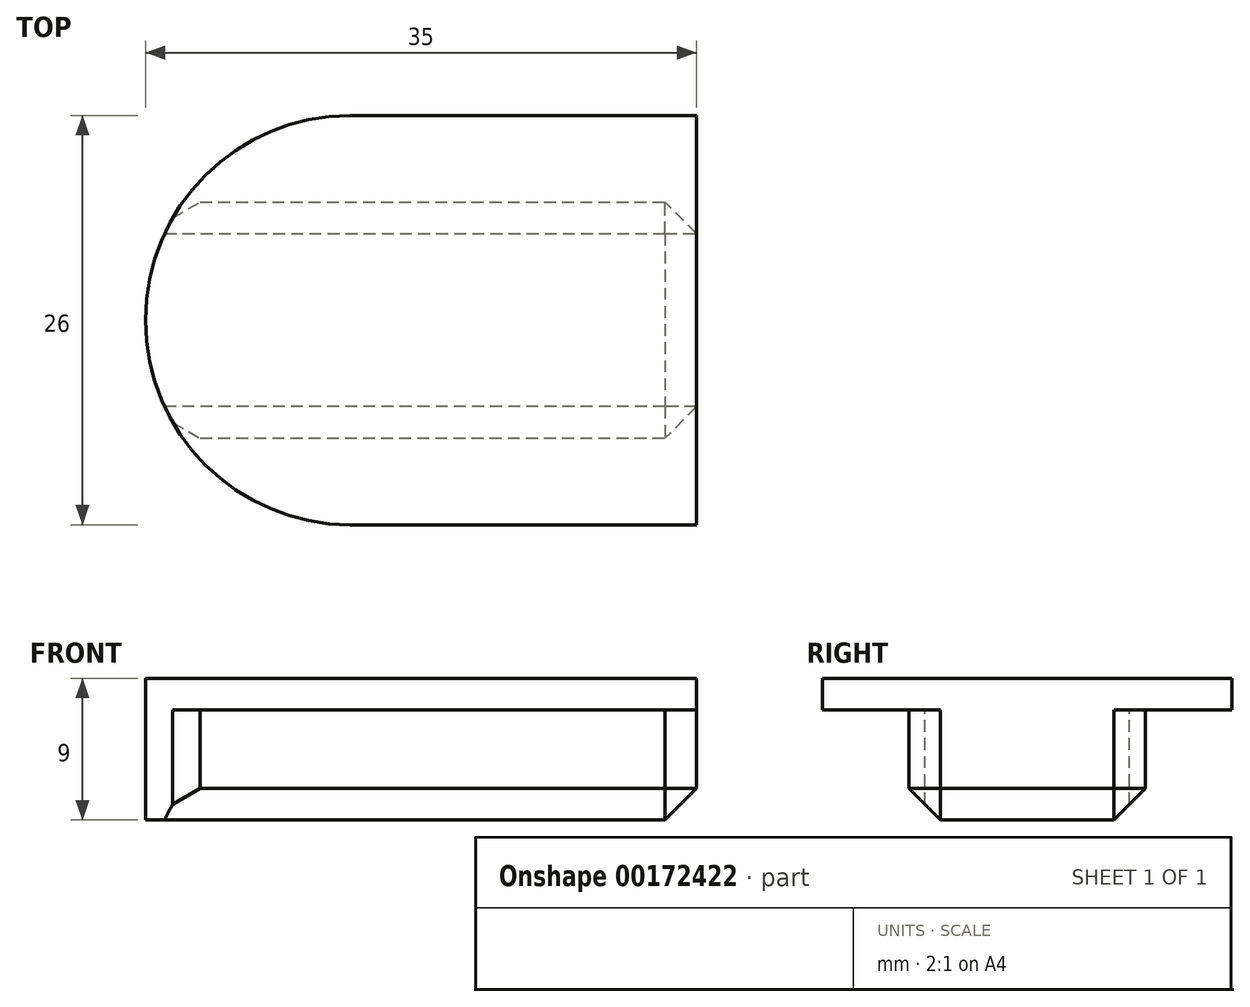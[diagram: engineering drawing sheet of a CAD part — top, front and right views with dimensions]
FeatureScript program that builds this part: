
annotation { "Feature Type Name" : "Feature", "Feature Type Description" : "" }
export const myFeature = defineFeature(function(context is Context, id is Id, definition is map)
    precondition{}
    {
        {
            var Q0;
            Q0=qCreatedBy(makeId("Top.planeOp"),FACE);
            var sketch = newSketch(context, id + "F0", { "sketchPlane" : qUnion([Q0])});
            skLineSegment(sketch, "E0.bottom", {"start": v(-17.5, 13) * mm, "end": v(17.5, 13) * mm});
            skLineSegment(sketch, "E0.top", {"start": v(-17.5, -13) * mm, "end": v(17.5, -13) * mm});
            skLineSegment(sketch, "E0.left", {"start": v(-17.5, 13) * mm, "end": v(-17.5, -13) * mm});
            skLineSegment(sketch, "E0.right", {"start": v(17.5, 13) * mm, "end": v(17.5, -13) * mm});
            skPoint(sketch, "E0.middle", {"position": v(0, 0) * mm});
            skSolve(sketch);
        }
        {
            var Q0;
            Q0 = qSketchRegion(id + "F0", true);
            extrude(context, id + "F1", {"entities" : qUnion([Q0]), "depth" : 2 * mm});
        }
        {
            var Q0;
            Q0=makeQuery(id+"F1.opExtrude","CAP_FACE",FACE,{"disambiguationData":[OSD([sQuery(id+"F0.wireOp",EDGE,"E0.bottom"),sQuery(id+"F0.wireOp",EDGE,"E0.top"),sQuery(id+"F0.wireOp",EDGE,"E0.left"),sQuery(id+"F0.wireOp",EDGE,"E0.right")])],"isStart":true});
            var sketch = newSketch(context, id + "F2", { "sketchPlane" : qUnion([Q0])});
            skLineSegment(sketch, "E1.bottom", {"start": v(-17.5, 7.5) * mm, "end": v(17.5, 7.5) * mm});
            skLineSegment(sketch, "E1.top", {"start": v(-17.5, -7.5) * mm, "end": v(17.5, -7.5) * mm});
            skLineSegment(sketch, "E1.left", {"start": v(-17.5, 7.5) * mm, "end": v(-17.5, -7.5) * mm});
            skLineSegment(sketch, "E1.right", {"start": v(17.5, 7.5) * mm, "end": v(17.5, -7.5) * mm});
            skPoint(sketch, "E1.middle", {"position": v(0, 0) * mm});
            skSolve(sketch);
        }
        {
            var Q0;
            Q0 = qSketchRegion(id + "F2", true);
            extrude(context, id + "F3", {"entities" : qUnion([Q0]), "operationType" : NewBodyOperationType.ADD, "depth" : 7 * mm});
        }
        {
            var Q0;
            Q0=makeQuery(id+"F1.opExtrude","SWEPT_EDGE",EDGE,{"disambiguationData":[OSD([sQuery(id+"F0.wireOp",EDGE,"E0.bottom"),sQuery(id+"F0.wireOp",EDGE,"E0.left")])]});
            var Q1;
            Q1=makeQuery(id+"F1.opExtrude","SWEPT_EDGE",EDGE,{"disambiguationData":[OSD([sQuery(id+"F0.wireOp",EDGE,"E0.top"),sQuery(id+"F0.wireOp",EDGE,"E0.left")])]});
            fillet(context, id + "F4", {"entities" : qUnion([Q0, Q1]), "radius" : 13 * mm, "tangentPropagation" : true, "allowEdgeOverflow" : false});
        }
        {
            var Q0;
            Q0=makeQuery(id+"F3.opExtrude","CAP_EDGE",EDGE,{"disambiguationData":[OSD([sQuery(id+"F2.wireOp",EDGE,"E1.bottom")])],"isStart":false});
            var Q1;
            Q1=makeQuery(id+"F3.opExtrude","CAP_EDGE",EDGE,{"disambiguationData":[OSD([sQuery(id+"F2.wireOp",EDGE,"E1.top")])],"isStart":false});
            var Q2;
            Q2=makeQuery(id+"F3.opExtrude","CAP_EDGE",EDGE,{"disambiguationData":[OSD([sQuery(id+"F2.wireOp",EDGE,"E1.left")])],"isStart":false});
            var Q3;
            Q3=makeQuery(id+"F3.opExtrude","CAP_EDGE",EDGE,{"disambiguationData":[OSD([sQuery(id+"F2.wireOp",EDGE,"E1.right")])],"isStart":false});
            var Q4;
            {var subQ0=sQuery(id+"F0.wireOp",EDGE,"E0.left");var subQ1=sQuery(id+"F0.wireOp",EDGE,"E0.top");Q4=makeQuery(id+"F3.boolean.opBoolean","SPLIT",EDGE,{"disambiguationData":[TD([makeQuery(id+"F1.opExtrude","SWEPT_FACE",FACE,{"disambiguationData":[OSD([subQ1])]})])],"derivedFrom":makeQuery(id+"F1.opExtrude","CAP_EDGE",EDGE,{"disambiguationData":[OSD([subQ0])],"isStart":true})});}
            var Q5;
            {var subQ0=sQuery(id+"F0.wireOp",EDGE,"E0.left");var subQ1=sQuery(id+"F0.wireOp",EDGE,"E0.bottom");Q5=makeQuery(id+"F3.boolean.opBoolean","SPLIT",EDGE,{"disambiguationData":[TD([makeQuery(id+"F1.opExtrude","SWEPT_FACE",FACE,{"disambiguationData":[OSD([subQ1])]})])],"derivedFrom":makeQuery(id+"F1.opExtrude","CAP_EDGE",EDGE,{"disambiguationData":[OSD([subQ0])],"isStart":true})});}
            var Q6;
            Q6=makeQuery(id+"F3.opExtrude","SWEPT_EDGE",EDGE,{"disambiguationData":[OSD([sQuery(id+"F0.wireOp",EDGE,"E0.left"),sQuery(id+"F2.wireOp",EDGE,"E1.bottom"),sQuery(id+"F2.wireOp",EDGE,"E1.left")])]});
            var Q7;
            Q7=makeQuery(id+"F3.opExtrude","SWEPT_EDGE",EDGE,{"disambiguationData":[OSD([sQuery(id+"F0.wireOp",EDGE,"E0.left"),sQuery(id+"F2.wireOp",EDGE,"E1.top"),sQuery(id+"F2.wireOp",EDGE,"E1.left")])]});
            var Q8;
            Q8=makeQuery(id+"F3.opExtrude","SWEPT_EDGE",EDGE,{"disambiguationData":[OSD([sQuery(id+"F0.wireOp",EDGE,"E0.right"),sQuery(id+"F2.wireOp",EDGE,"E1.bottom"),sQuery(id+"F2.wireOp",EDGE,"E1.right")])]});
            var Q9;
            Q9=makeQuery(id+"F3.opExtrude","SWEPT_EDGE",EDGE,{"disambiguationData":[OSD([sQuery(id+"F0.wireOp",EDGE,"E0.right"),sQuery(id+"F2.wireOp",EDGE,"E1.top"),sQuery(id+"F2.wireOp",EDGE,"E1.right")])]});
            var Q10;
            Q10=makeQuery(id+"F4.opFillet","BLEND_EDGE",EDGE,{"blendedFrom":[makeQuery(id+"F1.opExtrude","SWEPT_EDGE",EDGE,{"disambiguationData":[OSD([sQuery(id+"F0.wireOp",EDGE,"E0.bottom"),sQuery(id+"F0.wireOp",EDGE,"E0.left")])]}),makeQuery(id+"F3.opExtrude","SWEPT_FACE",FACE,{"disambiguationData":[OSD([sQuery(id+"F2.wireOp",EDGE,"E1.top")])]})],"blendedInto":[makeQuery(id+"F3.opExtrude","SWEPT_FACE",FACE,{"disambiguationData":[OSD([sQuery(id+"F2.wireOp",EDGE,"E1.top")])]})]});
            var Q11;
            Q11=makeQuery(id+"F4.opFillet","BLEND_EDGE",EDGE,{"blendedFrom":[makeQuery(id+"F1.opExtrude","SWEPT_EDGE",EDGE,{"disambiguationData":[OSD([sQuery(id+"F0.wireOp",EDGE,"E0.top"),sQuery(id+"F0.wireOp",EDGE,"E0.left")])]}),makeQuery(id+"F3.opExtrude","SWEPT_FACE",FACE,{"disambiguationData":[OSD([sQuery(id+"F2.wireOp",EDGE,"E1.bottom")])]})],"blendedInto":[makeQuery(id+"F3.opExtrude","SWEPT_FACE",FACE,{"disambiguationData":[OSD([sQuery(id+"F2.wireOp",EDGE,"E1.bottom")])]})]});
            var Q12;
            Q12=makeQuery(id+"F4.opFillet","BLEND_EDGE",EDGE,{"blendedFrom":[makeQuery(id+"F1.opExtrude","SWEPT_EDGE",EDGE,{"disambiguationData":[OSD([sQuery(id+"F0.wireOp",EDGE,"E0.top"),sQuery(id+"F0.wireOp",EDGE,"E0.left")])]}),makeQuery(id+"F3.opExtrude","CAP_FACE",FACE,{"disambiguationData":[OSD([sQuery(id+"F2.wireOp",EDGE,"E1.bottom"),sQuery(id+"F2.wireOp",EDGE,"E1.top"),sQuery(id+"F2.wireOp",EDGE,"E1.left"),sQuery(id+"F2.wireOp",EDGE,"E1.right")])],"isStart":false})],"blendedInto":[makeQuery(id+"F3.opExtrude","CAP_FACE",FACE,{"disambiguationData":[OSD([sQuery(id+"F2.wireOp",EDGE,"E1.bottom"),sQuery(id+"F2.wireOp",EDGE,"E1.top"),sQuery(id+"F2.wireOp",EDGE,"E1.left"),sQuery(id+"F2.wireOp",EDGE,"E1.right")])],"isStart":false})]});
            chamfer(context, id + "F5", {"entities" : qUnion([Q0, Q1, Q2, Q3, Q4, Q5, Q6, Q7, Q8, Q9, Q10, Q11, Q12]), "width" : 2 * mm, "tangentPropagation" : true});
        }
    });
